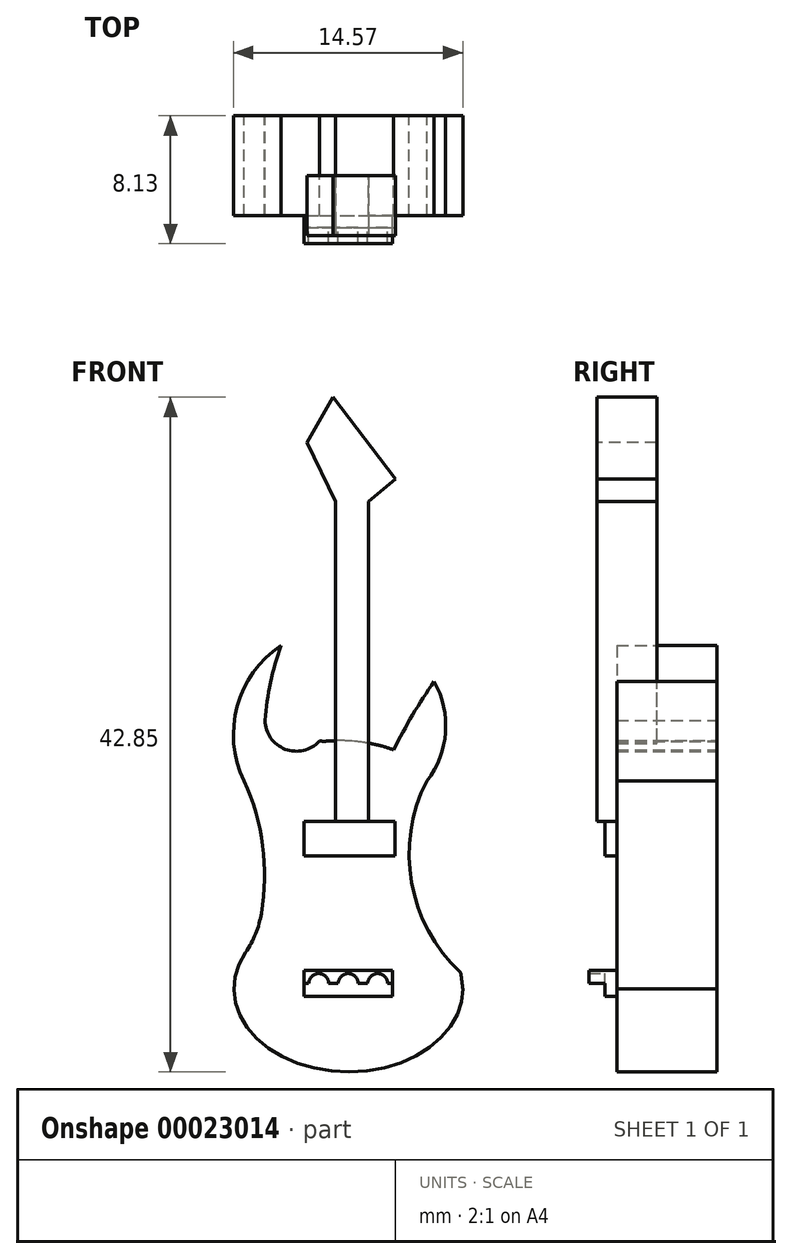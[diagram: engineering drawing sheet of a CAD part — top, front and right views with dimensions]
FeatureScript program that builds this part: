
annotation { "Feature Type Name" : "Feature", "Feature Type Description" : "" }
export const myFeature = defineFeature(function(context is Context, id is Id, definition is map)
    precondition{}
    {
        {
            var Q0;
            Q0=qCreatedBy(makeId("Front.planeOp"),FACE);
            var sketch = newSketch(context, id + "F0", { "sketchPlane" : qUnion([Q0])});
            skLineSegment(sketch, "E0.bottom", {"start": v(-22.78, 27.74) * mm, "end": v(28.02, 27.74) * mm});
            skLineSegment(sketch, "E0.top", {"start": v(-22.78, -23.06) * mm, "end": v(28.02, -23.06) * mm});
            skLineSegment(sketch, "E0.left", {"start": v(-22.78, 27.74) * mm, "end": v(-22.78, -23.06) * mm});
            skLineSegment(sketch, "E0.right", {"start": v(28.02, 27.74) * mm, "end": v(28.02, -23.06) * mm});
            skEllipticalArc(sketch, "E1", {});
            skEllipticalArc(sketch, "E2", {});
            skArc(sketch, "E3", {"start": v(-15.93, -12.29) * mm, "mid": v(-15.85, -8) * mm, "end": v(-17.03, -3.88) * mm});
            skArc(sketch, "E4", {"start": v(-3.14, -17.1) * mm, "mid": v(-3.2, -16.58) * mm, "end": v(-3.28, -16.07) * mm});
            skPoint(sketch, "E5.orphan", {"position": v(-17.67, -17.1) * mm});
            skArc(sketch, "E6", {"start": v(-14.7, 4.7) * mm, "mid": v(-17.47, 0.85) * mm, "end": v(-17.03, -3.88) * mm});
            skArc(sketch, "E7", {"start": v(-14.7, 4.7) * mm, "mid": v(-15.35, 2.37) * mm, "end": v(-15.7, -0.04) * mm});
            skArc(sketch, "E8", {"start": v(-15.75, 0) * mm, "mid": v(-15.72, -0.02) * mm, "end": v(-15.7, -0.04) * mm});
            skArc(sketch, "E9", {"start": v(-5.42, -3.88) * mm, "mid": v(-4.24, -0.8) * mm, "end": v(-4.96, 2.43) * mm});
            skPoint(sketch, "E10.visualSharp", {"position": v(-16.35, -14.07) * mm});
            skArc(sketch, "E10.filletArc", {"start": v(-16.93, -14.77) * mm, "mid": v(-16.3, -13.58) * mm, "end": v(-15.93, -12.29) * mm});
            skEllipticalArc(sketch, "E11.trimOffspring", {});
            skArc(sketch, "E12.trimOffspring", {"start": v(-12.26, -1.36) * mm, "mid": v(-11.74, -1.36) * mm, "end": v(-11.23, -1.32) * mm});
            skPoint(sketch, "E13.orphan", {"position": v(-15.75, -2.27) * mm});
            skArc(sketch, "E14", {"start": v(-15.7, -0.04) * mm, "mid": v(-14.43, -1.87) * mm, "end": v(-12.26, -1.36) * mm});
            skArc(sketch, "E15", {"start": v(-4.96, 2.43) * mm, "mid": v(-6.32, 0.31) * mm, "end": v(-7.53, -1.9) * mm});
            skArc(sketch, "E16", {"start": v(-5.42, -3.88) * mm, "mid": v(-6.4, -10.33) * mm, "end": v(-3.28, -16.06) * mm});
            skPoint(sketch, "E17.visualSharp", {"position": v(-3.28, -16.06) * mm});
            skArc(sketch, "E17.filletArc", {"start": v(-3.28, -16.07) * mm, "mid": v(-3.28, -16.07) * mm, "end": v(-3.28, -16.06) * mm});
            const initialGuessF0  = {"E1": [-0.010403777472674847, -0.017091918736696243, 1, 0, 0.007266130531206727, 0.005269959568753857, 2.6863592244006536, 0.19619956159554103], "E2": [-0.011229473166167736, -0.0038807739038020372, 1, 0, 0.005804891969514289, 0.0025654206563794336, 0, 1.7484858510245744], "E11.trimOffspring": [-0.011229473166167736, -0.0038807739038020372, 1, 0, 0.005804891969514287, 0.0025654206563794336, 3.141592653589793, 3.505684053848334]};
            skSetInitialGuess(sketch, initialGuessF0);
            skSolve(sketch);
        }
        {
            var Q0;
            {var subQ0=sQuery(id+"F0.wireOp",EDGE,"E6");Q0=makeQuery(id+"F0.imprint","IMPRINT",FACE,{"disambiguationData":[TD([[makeQuery(id+"F0.imprint","IMPRINT",EDGE,{"derivedFrom":subQ0}),1.0]])]});}
            var Q1;
            {var subQ1=sQuery(id+"F0.wireOp",EDGE,"E9");Q1=makeQuery(id+"F0.imprint","IMPRINT",FACE,{"disambiguationData":[TD([[makeQuery(id+"F0.imprint","IMPRINT",EDGE,{"derivedFrom":subQ1}),1.0]])]});}
            extrude(context, id + "F1", {"entities" : qUnion([Q0, Q1]), "depth" : 6.35 * mm});
        }
        {
            var Q0;
            Q0=makeQuery(id+"F1.opExtrude","CAP_FACE",FACE,{"disambiguationData":[OSD([sQuery(id+"F0.wireOp",EDGE,"E1"),sQuery(id+"F0.wireOp",EDGE,"E2"),sQuery(id+"F0.wireOp",EDGE,"E3"),sQuery(id+"F0.wireOp",EDGE,"E4"),sQuery(id+"F0.wireOp",EDGE,"E6"),sQuery(id+"F0.wireOp",EDGE,"E7"),sQuery(id+"F0.wireOp",EDGE,"E9"),sQuery(id+"F0.wireOp",EDGE,"E10.filletArc"),sQuery(id+"F0.wireOp",EDGE,"E12.trimOffspring"),sQuery(id+"F0.wireOp",EDGE,"E14"),sQuery(id+"F0.wireOp",EDGE,"E15")])],"isStart":false});
            var sketch = newSketch(context, id + "F2", { "sketchPlane" : qUnion([Q0])});
            skLineSegment(sketch, "E18.bottom", {"start": v(-12.86, -19.9) * mm, "end": v(-7.73, -19.9) * mm});
            skLineSegment(sketch, "E18.top", {"start": v(-12.86, -21.3) * mm, "end": v(-7.73, -21.3) * mm});
            skLineSegment(sketch, "E18.left", {"start": v(-12.86, -19.9) * mm, "end": v(-12.86, -21.3) * mm});
            skLineSegment(sketch, "E18.right", {"start": v(-7.73, -19.9) * mm, "end": v(-7.73, -21.3) * mm});
            skLineSegment(sketch, "E19.bottom", {"start": v(-12.86, -8.48) * mm, "end": v(-7.03, -8.48) * mm});
            skLineSegment(sketch, "E19.top", {"start": v(-12.86, -6.85) * mm, "end": v(-7.03, -6.85) * mm});
            skLineSegment(sketch, "E19.left", {"start": v(-12.86, -8.48) * mm, "end": v(-12.86, -6.85) * mm});
            skLineSegment(sketch, "E19.right", {"start": v(-7.03, -8.48) * mm, "end": v(-7.03, -6.85) * mm});
            skLineSegment(sketch, "E20.bottom", {"start": v(-11.23, -6.45) * mm, "end": v(-9.13, -6.45) * mm});
            skLineSegment(sketch, "E20.top", {"start": v(-11.23, 13.87) * mm, "end": v(-9.13, 13.87) * mm});
            skLineSegment(sketch, "E20.left", {"start": v(-11.23, -6.45) * mm, "end": v(-11.23, 13.87) * mm});
            skLineSegment(sketch, "E20.right", {"start": v(-9.13, -6.45) * mm, "end": v(-9.13, 13.87) * mm});
            skLineSegment(sketch, "E21.bottom", {"start": v(-27.08, -30.31) * mm, "end": v(23.72, -30.31) * mm});
            skLineSegment(sketch, "E21.top", {"start": v(-27.08, 20.49) * mm, "end": v(23.72, 20.49) * mm});
            skLineSegment(sketch, "E21.left", {"start": v(-27.08, -30.31) * mm, "end": v(-27.08, 20.49) * mm});
            skLineSegment(sketch, "E21.right", {"start": v(23.72, -30.31) * mm, "end": v(23.72, 20.49) * mm});
            skLineSegment(sketch, "E22", {"start": v(-11.23, 13.87) * mm, "end": v(-13.05, 17.6) * mm});
            skLineSegment(sketch, "E23", {"start": v(-13.05, 17.6) * mm, "end": v(-11.4, 20.49) * mm});
            skLineSegment(sketch, "E24", {"start": v(-11.4, 20.49) * mm, "end": v(-7.43, 15.28) * mm});
            skLineSegment(sketch, "E25", {"start": v(-7.43, 15.28) * mm, "end": v(-9.13, 13.87) * mm});
            skSolve(sketch);
        }
        {
            var Q0;
            {var subQ5=sQuery(id+"F2.wireOp",EDGE,"E20.top");Q0=makeQuery(id+"F2.imprint","IMPRINT",FACE,{"disambiguationData":[TD([[makeQuery(id+"F2.imprint","IMPRINT",EDGE,{"derivedFrom":subQ5}),-1.0]])]});}
            var Q1;
            Q1=makeQuery(id+"F2.imprint","IMPRINT",FACE,{"disambiguationData":[TD([[makeQuery(id+"F2.imprint","IMPRINT",EDGE,{"derivedFrom":sQuery(id+"F2.wireOp",EDGE,"E20.top")}),1.0]])]});
            var Q2;
            {var subQ5=sQuery(id+"F2.wireOp",EDGE,"E20.bottom");Q2=makeQuery(id+"F2.imprint","IMPRINT",FACE,{"disambiguationData":[TD([[makeQuery(id+"F2.imprint","IMPRINT",EDGE,{"derivedFrom":subQ5}),1.0]])]});}
            extrude(context, id + "F3", {"entities" : qUnion([Q0, Q1, Q2]), "operationType" : NewBodyOperationType.ADD, "oppositeDirection" : true, "depth" : 2.54 * mm, "hasSecondDirection" : true, "secondDirectionOppositeDirection" : false, "secondDirectionDepth" : 1.27 * mm});
        }
        {
            var Q0;
            Q0=makeQuery(id+"F1.opExtrude","CAP_FACE",FACE,{"disambiguationData":[OSD([sQuery(id+"F0.wireOp",EDGE,"E1"),sQuery(id+"F0.wireOp",EDGE,"E2"),sQuery(id+"F0.wireOp",EDGE,"E3"),sQuery(id+"F0.wireOp",EDGE,"E4"),sQuery(id+"F0.wireOp",EDGE,"E6"),sQuery(id+"F0.wireOp",EDGE,"E7"),sQuery(id+"F0.wireOp",EDGE,"E9"),sQuery(id+"F0.wireOp",EDGE,"E10.filletArc"),sQuery(id+"F0.wireOp",EDGE,"E12.trimOffspring"),sQuery(id+"F0.wireOp",EDGE,"E14"),sQuery(id+"F0.wireOp",EDGE,"E15")])],"isStart":false});
            var sketch = newSketch(context, id + "F4", { "sketchPlane" : qUnion([Q0])});
            skLineSegment(sketch, "E26.bottom", {"start": v(-13.23, -6.45) * mm, "end": v(-7.45, -6.45) * mm});
            skLineSegment(sketch, "E26.top", {"start": v(-13.23, -8.66) * mm, "end": v(-7.45, -8.66) * mm});
            skLineSegment(sketch, "E26.left", {"start": v(-13.23, -6.45) * mm, "end": v(-13.23, -8.66) * mm});
            skLineSegment(sketch, "E26.right", {"start": v(-7.45, -6.45) * mm, "end": v(-7.45, -8.66) * mm});
            skLineSegment(sketch, "E27.bottom", {"start": v(-13.23, -15.93) * mm, "end": v(-7.61, -15.93) * mm});
            skLineSegment(sketch, "E27.top", {"start": v(-13.23, -17.58) * mm, "end": v(-7.61, -17.58) * mm});
            skLineSegment(sketch, "E27.left", {"start": v(-13.23, -15.93) * mm, "end": v(-13.23, -17.58) * mm});
            skLineSegment(sketch, "E27.right", {"start": v(-7.61, -15.93) * mm, "end": v(-7.61, -17.58) * mm});
            skSolve(sketch);
        }
        {
            var Q0;
            Q0=makeQuery(id+"F4.imprint","IMPRINT",FACE,{"disambiguationData":[TD([[makeQuery(id+"F4.imprint","IMPRINT",EDGE,{"derivedFrom":sQuery(id+"F4.wireOp",EDGE,"E26.top")}),1.0]])]});
            var Q1;
            Q1=makeQuery(id+"F4.imprint","IMPRINT",FACE,{"disambiguationData":[TD([[makeQuery(id+"F4.imprint","IMPRINT",EDGE,{"derivedFrom":sQuery(id+"F4.wireOp",EDGE,"E27.bottom")}),-1.0]])]});
            extrude(context, id + "F5", {"entities" : qUnion([Q0, Q1]), "operationType" : NewBodyOperationType.ADD, "depth" : 0.76 * mm});
        }
        {
            var Q0;
            Q0=makeQuery(id+"F5.opExtrude","CAP_FACE",FACE,{"disambiguationData":[OSD([sQuery(id+"F4.wireOp",EDGE,"E27.bottom"),sQuery(id+"F4.wireOp",EDGE,"E27.top"),sQuery(id+"F4.wireOp",EDGE,"E27.left"),sQuery(id+"F4.wireOp",EDGE,"E27.right")])],"isStart":false});
            var sketch = newSketch(context, id + "F6", { "sketchPlane" : qUnion([Q0])});
            skCircle(sketch, "E28", {"center": v(-49.29, -12.29) * mm, "radius": 0.56 * mm});
            skLineSegment(sketch, "E29", {"start": v(-10.42, -15.93) * mm, "end": v(-10.42, -16.75) * mm});
            skLineSegment(sketch, "E30", {"start": v(-10.42, -16.75) * mm, "end": v(-13.23, -16.75) * mm});
            skLineSegment(sketch, "E31", {"start": v(-13.23, -16.75) * mm, "end": v(-7.61, -16.75) * mm});
            skLineSegment(sketch, "E32", {"start": v(-13.23, -16.75) * mm, "end": v(-11.36, -16.75) * mm});
            skLineSegment(sketch, "E33", {"start": v(-11.36, -16.75) * mm, "end": v(-9.48, -16.75) * mm});
            skLineSegment(sketch, "E34", {"start": v(-9.48, -16.75) * mm, "end": v(-7.61, -16.75) * mm});
            skCircle(sketch, "E35", {"center": v(-10.42, -16.75) * mm, "radius": 0.64 * mm});
            skCircle(sketch, "E36", {"center": v(-12.3, -16.75) * mm, "radius": 0.64 * mm});
            skCircle(sketch, "E37", {"center": v(-8.55, -16.75) * mm, "radius": 0.64 * mm});
            skSolve(sketch);
        }
        {
            var Q0;
            {var subQ0=sQuery(id+"F6.wireOp",EDGE,"E36");var subQ1=sQuery(id+"F6.wireOp",EDGE,"E32");var subQ3=makeQuery(id+"F6.imprint","INTERSECT",VERTEX,{"disambiguationData":[OD(0.0)],"derivedFrom":[subQ1,subQ0]});Q0=makeQuery(id+"F6.imprint","IMPRINT",FACE,{"disambiguationData":[TD([[makeQuery(id+"F6.imprint","IMPRINT",EDGE,{"disambiguationData":[TD([[subQ3,-1.0]])],"derivedFrom":subQ1}),1.0]])]});}
            var Q1;
            {var subQ0=sQuery(id+"F6.wireOp",EDGE,"E36");var subQ1=sQuery(id+"F6.wireOp",EDGE,"E32");var subQ3=makeQuery(id+"F6.imprint","INTERSECT",VERTEX,{"disambiguationData":[OD(0.0)],"derivedFrom":[subQ1,subQ0]});Q1=makeQuery(id+"F6.imprint","IMPRINT",FACE,{"disambiguationData":[TD([[makeQuery(id+"F6.imprint","IMPRINT",EDGE,{"disambiguationData":[TD([[subQ3,-1.0]])],"derivedFrom":subQ1}),-1.0]])]});}
            var Q2;
            {var subQ1=sQuery(id+"F6.wireOp",EDGE,"E33");var subQ3=sQuery(id+"F6.wireOp",EDGE,"E29");var subQ5=makeQuery(id+"F6.imprint","INTERSECT",VERTEX,{"derivedFrom":[subQ3,subQ1]});Q2=makeQuery(id+"F6.imprint","IMPRINT",FACE,{"disambiguationData":[TD([[makeQuery(id+"F6.imprint","IMPRINT",EDGE,{"disambiguationData":[TD([[subQ5,1.0]])],"derivedFrom":subQ3}),-1.0]])]});}
            var Q3;
            {var subQ1=sQuery(id+"F6.wireOp",EDGE,"E33");var subQ3=sQuery(id+"F6.wireOp",EDGE,"E29");var subQ5=makeQuery(id+"F6.imprint","INTERSECT",VERTEX,{"derivedFrom":[subQ3,subQ1]});Q3=makeQuery(id+"F6.imprint","IMPRINT",FACE,{"disambiguationData":[TD([[makeQuery(id+"F6.imprint","IMPRINT",EDGE,{"disambiguationData":[TD([[subQ5,1.0]])],"derivedFrom":subQ3}),1.0]])]});}
            var Q4;
            {var subQ1=sQuery(id+"F6.wireOp",EDGE,"E33");var subQ4=makeQuery(id+"F6.imprint","INTERSECT",VERTEX,{"derivedFrom":[sQuery(id+"F6.wireOp",EDGE,"E29"),subQ1]});Q4=makeQuery(id+"F6.imprint","IMPRINT",FACE,{"disambiguationData":[TD([[makeQuery(id+"F6.imprint","IMPRINT",EDGE,{"disambiguationData":[TD([[subQ4,1.0]])],"derivedFrom":subQ1}),-1.0]])]});}
            var Q5;
            {var subQ0=sQuery(id+"F6.wireOp",EDGE,"E37");var subQ1=sQuery(id+"F6.wireOp",EDGE,"E34");var subQ3=makeQuery(id+"F6.imprint","INTERSECT",VERTEX,{"disambiguationData":[OD(0.0)],"derivedFrom":[subQ1,subQ0]});Q5=makeQuery(id+"F6.imprint","IMPRINT",FACE,{"disambiguationData":[TD([[makeQuery(id+"F6.imprint","IMPRINT",EDGE,{"disambiguationData":[TD([[subQ3,-1.0]])],"derivedFrom":subQ1}),1.0]])]});}
            var Q6;
            {var subQ0=sQuery(id+"F6.wireOp",EDGE,"E37");var subQ1=sQuery(id+"F6.wireOp",EDGE,"E34");var subQ3=makeQuery(id+"F6.imprint","INTERSECT",VERTEX,{"disambiguationData":[OD(0.0)],"derivedFrom":[subQ1,subQ0]});Q6=makeQuery(id+"F6.imprint","IMPRINT",FACE,{"disambiguationData":[TD([[makeQuery(id+"F6.imprint","IMPRINT",EDGE,{"disambiguationData":[TD([[subQ3,-1.0]])],"derivedFrom":subQ1}),-1.0]])]});}
            extrude(context, id + "F7", {"entities" : qUnion([Q0, Q1, Q2, Q3, Q4, Q5, Q6]), "operationType" : NewBodyOperationType.ADD, "depth" : 1.02 * mm});
        }
    });
